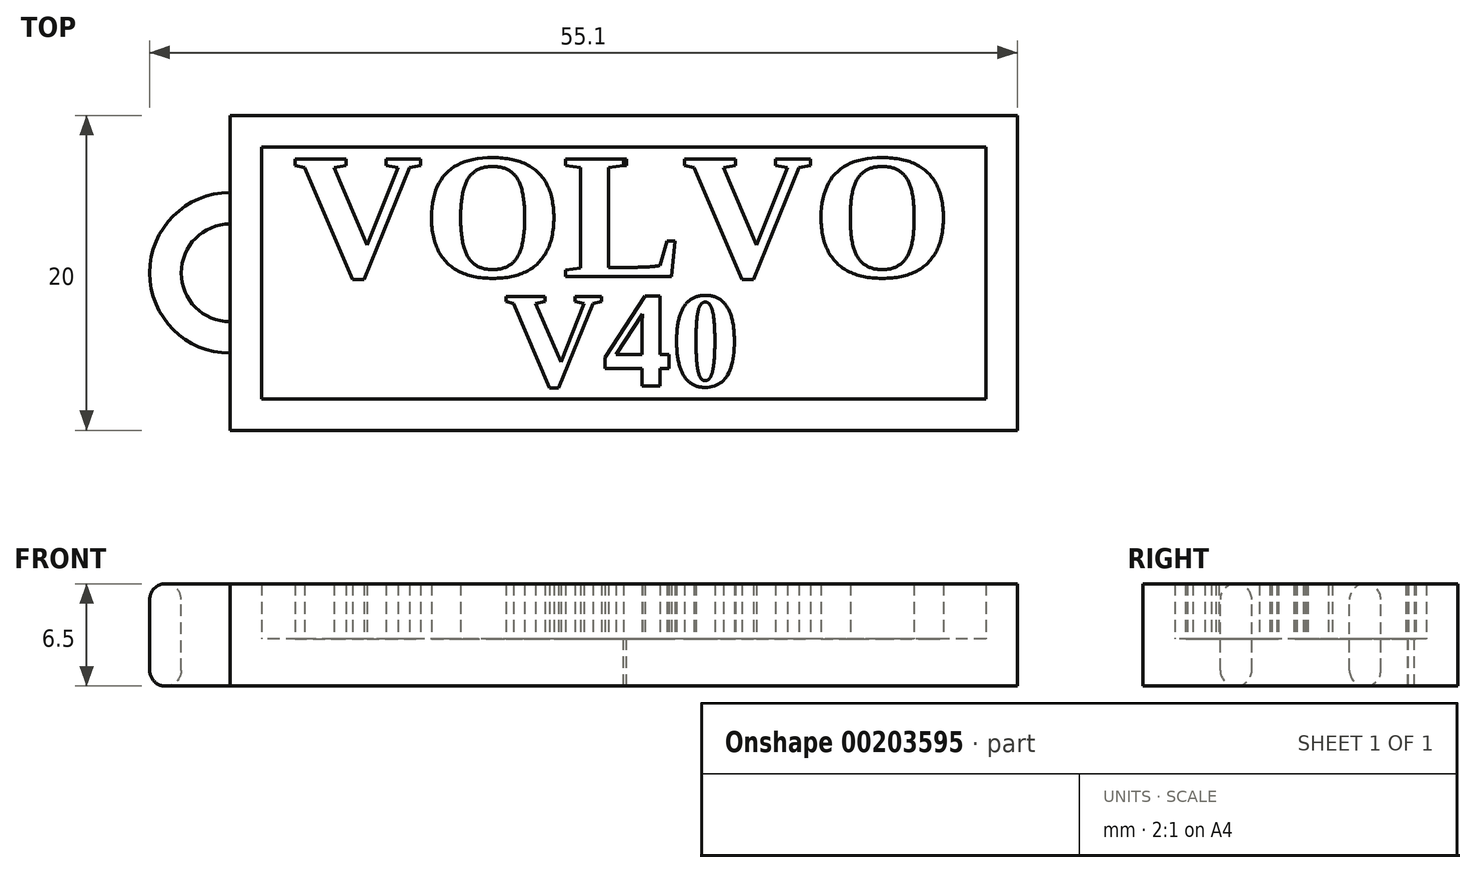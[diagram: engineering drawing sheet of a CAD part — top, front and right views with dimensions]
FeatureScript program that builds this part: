
annotation { "Feature Type Name" : "Feature", "Feature Type Description" : "" }
export const myFeature = defineFeature(function(context is Context, id is Id, definition is map)
    precondition{}
    {
        {
            var Q0;
            Q0=qCreatedBy(makeId("Top.planeOp"),FACE);
            var sketch = newSketch(context, id + "F0", { "sketchPlane" : qUnion([Q0])});
            skLineSegment(sketch, "E0.bottom", {"start": v(25, 10) * mm, "end": v(-25, 10) * mm});
            skLineSegment(sketch, "E0.top", {"start": v(25, -10) * mm, "end": v(-25, -10) * mm});
            skLineSegment(sketch, "E0.left", {"start": v(25, 10) * mm, "end": v(25, -10) * mm});
            skLineSegment(sketch, "E0.right", {"start": v(-25, 10) * mm, "end": v(-25, -10) * mm});
            skPoint(sketch, "E0.middle", {"position": v(0, 0) * mm});
            skArc(sketch, "E1", {"start": v(-25, 5.1) * mm, "mid": v(-30.1, 0) * mm, "end": v(-25, -5.1) * mm});
            skArc(sketch, "E2.0", {"start": v(-25, 3.1) * mm, "mid": v(-28.1, 0) * mm, "end": v(-25, -3.1) * mm});
            skLineSegment(sketch, "E3", {"start": v(0, 10) * mm, "end": v(0, -10) * mm});
            skLineSegment(sketch, "E4", {"start": v(-25, 0) * mm, "end": v(25, 0) * mm, "construction": true});
            skText(sketch, "E5", { "text": "V40", "fontName": "Tinos-Bold.ttf"});
            skLineSegment(sketch, "E6.0", {"start": v(-23, 8) * mm, "end": v(-23, -8) * mm});
            skLineSegment(sketch, "E6.1", {"start": v(23, 8) * mm, "end": v(-23, 8) * mm});
            skLineSegment(sketch, "E6.2", {"start": v(23, 8) * mm, "end": v(23, -8) * mm});
            skLineSegment(sketch, "E6.3", {"start": v(23, -8) * mm, "end": v(-23, -8) * mm});
            skText(sketch, "E7", { "text": "VOLVO", "fontName": "Tinos-Bold.ttf"});
            const initialGuessF0  = {"E5": [-0.00756, -0.00719, 1, 0, 0.00624], "E7": [-0.021, -0.00024, 1, 0, 0.00822]};
            skSetInitialGuess(sketch, initialGuessF0);
            skSolve(sketch);
        }
        {
            var Q0;
            {var subQ0=sQuery(id+"F0.wireOp",EDGE,"E1");Q0=makeQuery(id+"F0.imprint","IMPRINT",FACE,{"disambiguationData":[TD([[makeQuery(id+"F0.imprint","IMPRINT",EDGE,{"derivedFrom":subQ0}),1.0]])]});}
            var Q1;
            {var subQ0=sQuery(id+"F0.wireOp",EDGE,"E6.0");Q1=makeQuery(id+"F0.imprint","IMPRINT",FACE,{"disambiguationData":[TD([[makeQuery(id+"F0.imprint","IMPRINT",EDGE,{"derivedFrom":subQ0}),-1.0]])]});}
            var Q2;
            Q2=makeQuery(id+"F0.imprint","IMPRINT",FACE,{"disambiguationData":[TD([[makeQuery(id+"F0.imprint","IMPRINT",EDGE,{"derivedFrom":sQuery(id+"F0.wireOp",EDGE,"E5.sketch_text.stroke-0")}),1.0]])]});
            var Q3;
            {var subQ5=sQuery(id+"F0.wireOp",EDGE,"E0.left");Q3=makeQuery(id+"F0.imprint","IMPRINT",FACE,{"disambiguationData":[TD([[makeQuery(id+"F0.imprint","IMPRINT",EDGE,{"derivedFrom":subQ5}),-1.0]])]});}
            var Q4;
            Q4=makeQuery(id+"F0.imprint","IMPRINT",FACE,{"disambiguationData":[TD([[makeQuery(id+"F0.imprint","IMPRINT",EDGE,{"derivedFrom":sQuery(id+"F0.wireOp",EDGE,"E5.sketch_text.stroke-15")}),1.0]])]});
            var Q5;
            Q5=makeQuery(id+"F0.imprint","IMPRINT",FACE,{"disambiguationData":[TD([[makeQuery(id+"F0.imprint","IMPRINT",EDGE,{"derivedFrom":sQuery(id+"F0.wireOp",EDGE,"E7.sketch_text.stroke-60")}),-1.0]])]});
            var Q6;
            Q6=makeQuery(id+"F0.imprint","IMPRINT",FACE,{"disambiguationData":[TD([[makeQuery(id+"F0.imprint","IMPRINT",EDGE,{"derivedFrom":sQuery(id+"F0.wireOp",EDGE,"E7.sketch_text.stroke-60")}),1.0]])]});
            var Q7;
            Q7=makeQuery(id+"F0.imprint","IMPRINT",FACE,{"disambiguationData":[TD([[makeQuery(id+"F0.imprint","IMPRINT",EDGE,{"derivedFrom":sQuery(id+"F0.wireOp",EDGE,"E7.sketch_text.stroke-45")}),-1.0]])]});
            var Q8;
            Q8=makeQuery(id+"F0.imprint","IMPRINT",FACE,{"disambiguationData":[TD([[makeQuery(id+"F0.imprint","IMPRINT",EDGE,{"derivedFrom":sQuery(id+"F0.wireOp",EDGE,"E5.sketch_text.stroke-30")}),-1.0]])]});
            var Q9;
            Q9=makeQuery(id+"F0.imprint","IMPRINT",FACE,{"disambiguationData":[TD([[makeQuery(id+"F0.imprint","IMPRINT",EDGE,{"derivedFrom":sQuery(id+"F0.wireOp",EDGE,"E5.sketch_text.stroke-37")}),1.0]])]});
            var Q10;
            Q10=makeQuery(id+"F0.imprint","IMPRINT",FACE,{"disambiguationData":[TD([[makeQuery(id+"F0.imprint","IMPRINT",EDGE,{"derivedFrom":sQuery(id+"F0.wireOp",EDGE,"E5.sketch_text.stroke-15")}),-1.0]])]});
            var Q11;
            {var subQ5=sQuery(id+"F0.wireOp",EDGE,"E5.sketch_text.stroke-26");Q11=makeQuery(id+"F0.imprint","IMPRINT",FACE,{"disambiguationData":[TD([[makeQuery(id+"F0.imprint","IMPRINT",EDGE,{"derivedFrom":subQ5}),1.0]])]});}
            var Q12;
            {var subQ0=sQuery(id+"F0.wireOp",EDGE,"E5.sketch_text.stroke-27");var subQ1=sQuery(id+"F0.wireOp",EDGE,"E3");var subQ2=makeQuery(id+"F0.imprint","INTERSECT",VERTEX,{"derivedFrom":[subQ1,subQ0]});Q12=makeQuery(id+"F0.imprint","IMPRINT",FACE,{"disambiguationData":[TD([[makeQuery(id+"F0.imprint","IMPRINT",EDGE,{"disambiguationData":[TD([[subQ2,-1.0]])],"derivedFrom":subQ1}),-1.0]])]});}
            var Q13;
            {var subQ0=sQuery(id+"F0.wireOp",EDGE,"E5.sketch_text.stroke-19");Q13=makeQuery(id+"F0.imprint","IMPRINT",FACE,{"disambiguationData":[TD([[makeQuery(id+"F0.imprint","IMPRINT",EDGE,{"derivedFrom":subQ0}),-1.0]])]});}
            var Q14;
            Q14=makeQuery(id+"F0.imprint","IMPRINT",FACE,{"disambiguationData":[TD([[makeQuery(id+"F0.imprint","IMPRINT",EDGE,{"derivedFrom":sQuery(id+"F0.wireOp",EDGE,"E5.sketch_text.stroke-0")}),-1.0]])]});
            var Q15;
            {var subQ0=sQuery(id+"F0.wireOp",EDGE,"E7.sketch_text.stroke-33");Q15=makeQuery(id+"F0.imprint","IMPRINT",FACE,{"disambiguationData":[TD([[makeQuery(id+"F0.imprint","IMPRINT",EDGE,{"derivedFrom":subQ0}),-1.0]])]});}
            var Q16;
            {var subQ5=sQuery(id+"F0.wireOp",EDGE,"E7.sketch_text.stroke-31");Q16=makeQuery(id+"F0.imprint","IMPRINT",FACE,{"disambiguationData":[TD([[makeQuery(id+"F0.imprint","IMPRINT",EDGE,{"derivedFrom":subQ5}),1.0]])]});}
            var Q17;
            {var subQ4=sQuery(id+"F0.wireOp",EDGE,"E7.sketch_text.stroke-31");Q17=makeQuery(id+"F0.imprint","IMPRINT",FACE,{"disambiguationData":[TD([[makeQuery(id+"F0.imprint","IMPRINT",EDGE,{"derivedFrom":subQ4}),-1.0]])]});}
            var Q18;
            Q18=makeQuery(id+"F0.imprint","IMPRINT",FACE,{"disambiguationData":[TD([[makeQuery(id+"F0.imprint","IMPRINT",EDGE,{"derivedFrom":sQuery(id+"F0.wireOp",EDGE,"E7.sketch_text.stroke-15")}),-1.0]])]});
            var Q19;
            Q19=makeQuery(id+"F0.imprint","IMPRINT",FACE,{"disambiguationData":[TD([[makeQuery(id+"F0.imprint","IMPRINT",EDGE,{"derivedFrom":sQuery(id+"F0.wireOp",EDGE,"E7.sketch_text.stroke-15")}),1.0]])]});
            var Q20;
            Q20=makeQuery(id+"F0.imprint","IMPRINT",FACE,{"disambiguationData":[TD([[makeQuery(id+"F0.imprint","IMPRINT",EDGE,{"derivedFrom":sQuery(id+"F0.wireOp",EDGE,"E7.sketch_text.stroke-0")}),-1.0]])]});
            extrude(context, id + "F1", {"entities" : qUnion([Q0, Q1, Q2, Q3, Q4, Q5, Q6, Q7, Q8, Q9, Q10, Q11, Q12, Q13, Q14, Q15, Q16, Q17, Q18, Q19, Q20]), "oppositeDirection" : true, "depth" : 3 * mm});
        }
        {
            var Q0;
            {var subQ0=sQuery(id+"F0.wireOp",EDGE,"E6.0");Q0=makeQuery(id+"F0.imprint","IMPRINT",FACE,{"disambiguationData":[TD([[makeQuery(id+"F0.imprint","IMPRINT",EDGE,{"derivedFrom":subQ0}),-1.0]])]});}
            var Q1;
            {var subQ0=sQuery(id+"F0.wireOp",EDGE,"E1");Q1=makeQuery(id+"F0.imprint","IMPRINT",FACE,{"disambiguationData":[TD([[makeQuery(id+"F0.imprint","IMPRINT",EDGE,{"derivedFrom":subQ0}),1.0]])]});}
            var Q2;
            {var subQ5=sQuery(id+"F0.wireOp",EDGE,"E0.left");Q2=makeQuery(id+"F0.imprint","IMPRINT",FACE,{"disambiguationData":[TD([[makeQuery(id+"F0.imprint","IMPRINT",EDGE,{"derivedFrom":subQ5}),-1.0]])]});}
            var Q3;
            Q3=makeQuery(id+"F0.imprint","IMPRINT",FACE,{"disambiguationData":[TD([[makeQuery(id+"F0.imprint","IMPRINT",EDGE,{"derivedFrom":sQuery(id+"F0.wireOp",EDGE,"E7.sketch_text.stroke-60")}),-1.0]])]});
            var Q4;
            Q4=makeQuery(id+"F0.imprint","IMPRINT",FACE,{"disambiguationData":[TD([[makeQuery(id+"F0.imprint","IMPRINT",EDGE,{"derivedFrom":sQuery(id+"F0.wireOp",EDGE,"E7.sketch_text.stroke-45")}),-1.0]])]});
            var Q5;
            {var subQ4=sQuery(id+"F0.wireOp",EDGE,"E7.sketch_text.stroke-31");Q5=makeQuery(id+"F0.imprint","IMPRINT",FACE,{"disambiguationData":[TD([[makeQuery(id+"F0.imprint","IMPRINT",EDGE,{"derivedFrom":subQ4}),-1.0]])]});}
            var Q6;
            {var subQ0=sQuery(id+"F0.wireOp",EDGE,"E7.sketch_text.stroke-33");Q6=makeQuery(id+"F0.imprint","IMPRINT",FACE,{"disambiguationData":[TD([[makeQuery(id+"F0.imprint","IMPRINT",EDGE,{"derivedFrom":subQ0}),-1.0]])]});}
            var Q7;
            Q7=makeQuery(id+"F0.imprint","IMPRINT",FACE,{"disambiguationData":[TD([[makeQuery(id+"F0.imprint","IMPRINT",EDGE,{"derivedFrom":sQuery(id+"F0.wireOp",EDGE,"E7.sketch_text.stroke-0")}),-1.0]])]});
            var Q8;
            Q8=makeQuery(id+"F0.imprint","IMPRINT",FACE,{"disambiguationData":[TD([[makeQuery(id+"F0.imprint","IMPRINT",EDGE,{"derivedFrom":sQuery(id+"F0.wireOp",EDGE,"E7.sketch_text.stroke-15")}),-1.0]])]});
            var Q9;
            Q9=makeQuery(id+"F0.imprint","IMPRINT",FACE,{"disambiguationData":[TD([[makeQuery(id+"F0.imprint","IMPRINT",EDGE,{"derivedFrom":sQuery(id+"F0.wireOp",EDGE,"E5.sketch_text.stroke-0")}),-1.0]])]});
            var Q10;
            Q10=makeQuery(id+"F0.imprint","IMPRINT",FACE,{"disambiguationData":[TD([[makeQuery(id+"F0.imprint","IMPRINT",EDGE,{"derivedFrom":sQuery(id+"F0.wireOp",EDGE,"E5.sketch_text.stroke-15")}),-1.0]])]});
            var Q11;
            Q11=makeQuery(id+"F0.imprint","IMPRINT",FACE,{"disambiguationData":[TD([[makeQuery(id+"F0.imprint","IMPRINT",EDGE,{"derivedFrom":sQuery(id+"F0.wireOp",EDGE,"E5.sketch_text.stroke-30")}),-1.0]])]});
            var Q12;
            {var subQ0=sQuery(id+"F0.wireOp",EDGE,"E5.sketch_text.stroke-19");Q12=makeQuery(id+"F0.imprint","IMPRINT",FACE,{"disambiguationData":[TD([[makeQuery(id+"F0.imprint","IMPRINT",EDGE,{"derivedFrom":subQ0}),-1.0]])]});}
            extrude(context, id + "F2", {"entities" : qUnion([Q0, Q1, Q2, Q3, Q4, Q5, Q6, Q7, Q8, Q9, Q10, Q11, Q12]), "operationType" : NewBodyOperationType.ADD, "depth" : 3.5 * mm});
        }
        {
            var Q0;
            Q0=makeQuery(id+"F2.opExtrude","CAP_EDGE",EDGE,{"disambiguationData":[OSD([sQuery(id+"F0.wireOp",EDGE,"E2.0")])],"isStart":false});
            var Q1;
            Q1=makeQuery(id+"F2.opExtrude","CAP_EDGE",EDGE,{"disambiguationData":[OSD([sQuery(id+"F0.wireOp",EDGE,"E1")])],"isStart":false});
            var Q2;
            Q2=makeQuery(id+"F1.opExtrude","CAP_EDGE",EDGE,{"disambiguationData":[OSD([sQuery(id+"F0.wireOp",EDGE,"E1")])],"isStart":false});
            var Q3;
            Q3=makeQuery(id+"F1.opExtrude","CAP_EDGE",EDGE,{"disambiguationData":[OSD([sQuery(id+"F0.wireOp",EDGE,"E2.0")])],"isStart":false});
            fillet(context, id + "F3", {"entities" : qUnion([Q0, Q1, Q2, Q3]), "radius" : 1 * mm, "tangentPropagation" : true, "allowEdgeOverflow" : false});
        }
    });
